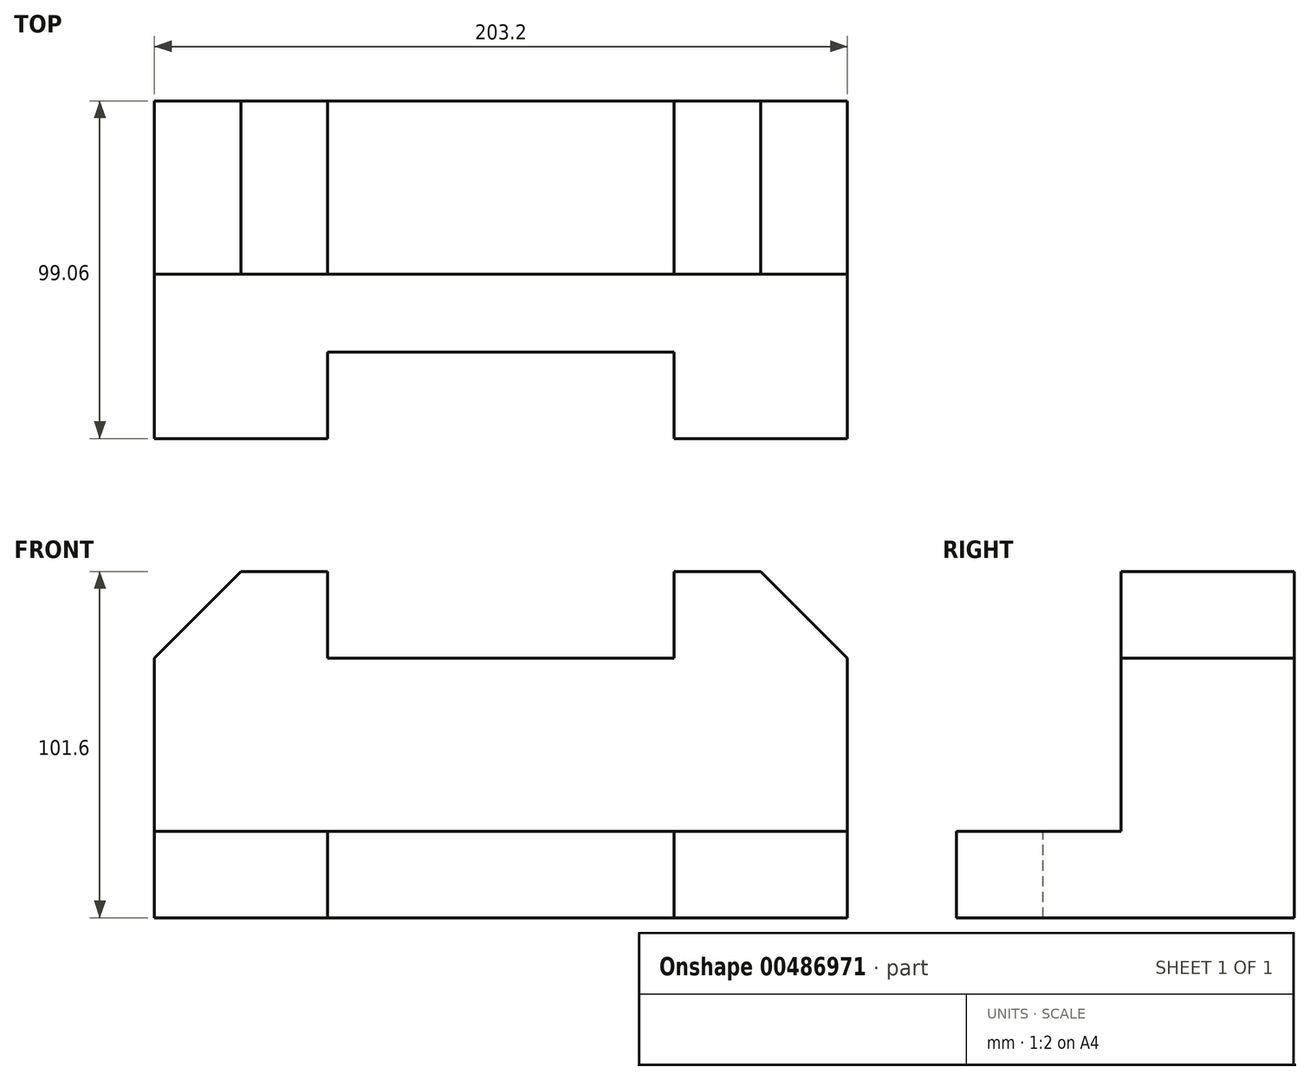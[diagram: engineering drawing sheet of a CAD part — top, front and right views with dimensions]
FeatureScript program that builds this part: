
annotation { "Feature Type Name" : "Feature", "Feature Type Description" : "" }
export const myFeature = defineFeature(function(context is Context, id is Id, definition is map)
    precondition{}
    {
        {
            var Q0;
            Q0=qCreatedBy(makeId("Front.planeOp"),FACE);
            var sketch = newSketch(context, id + "F0", { "sketchPlane" : qUnion([Q0])});
            skLineSegment(sketch, "E0.bottom", {"start": v(0, 0) * mm, "end": v(-203.2, 0) * mm});
            skLineSegment(sketch, "E0.top", {"start": v(0, 76.2) * mm, "end": v(-203.2, 76.2) * mm});
            skLineSegment(sketch, "E0.left", {"start": v(0, 0) * mm, "end": v(0, 76.2) * mm});
            skLineSegment(sketch, "E0.right", {"start": v(-203.2, 0) * mm, "end": v(-203.2, 76.2) * mm});
            skSolve(sketch);
        }
        {
            var Q0;
            Q0=makeQuery(id+"F0.imprint","IMPRINT",FACE,{"disambiguationData":[TD([[makeQuery(id+"F0.imprint","IMPRINT",EDGE,{"derivedFrom":sQuery(id+"F0.wireOp",EDGE,"E0.bottom")}),-1.0]])]});
            extrude(context, id + "F1", {"entities" : qUnion([Q0]), "depth" : 50.8 * mm});
        }
        {
            var Q0;
            Q0=makeQuery(id+"F1.opExtrude","SWEPT_FACE",FACE,{"disambiguationData":[OSD([sQuery(id+"F0.wireOp",EDGE,"E0.top")])]});
            var sketch = newSketch(context, id + "F2", { "sketchPlane" : qUnion([Q0])});
            skLineSegment(sketch, "E1.bottom", {"start": v(0, 0) * mm, "end": v(-50.8, 0) * mm});
            skLineSegment(sketch, "E1.top", {"start": v(0, -50.8) * mm, "end": v(-50.8, -50.8) * mm});
            skLineSegment(sketch, "E1.left", {"start": v(0, 0) * mm, "end": v(0, -50.8) * mm});
            skLineSegment(sketch, "E1.right", {"start": v(-50.8, 0) * mm, "end": v(-50.8, -50.8) * mm});
            skLineSegment(sketch, "E2.bottom", {"start": v(-203.2, 0) * mm, "end": v(-152.4, 0) * mm});
            skLineSegment(sketch, "E2.top", {"start": v(-203.2, -50.8) * mm, "end": v(-152.4, -50.8) * mm});
            skLineSegment(sketch, "E2.left", {"start": v(-203.2, 0) * mm, "end": v(-203.2, -50.8) * mm});
            skLineSegment(sketch, "E2.right", {"start": v(-152.4, 0) * mm, "end": v(-152.4, -50.8) * mm});
            skSolve(sketch);
        }
        {
            var Q0;
            Q0=makeQuery(id+"F2.imprint","IMPRINT",FACE,{"disambiguationData":[TD([[makeQuery(id+"F2.imprint","IMPRINT",EDGE,{"derivedFrom":sQuery(id+"F2.wireOp",EDGE,"E2.bottom")}),1.0]])]});
            var Q1;
            Q1=makeQuery(id+"F2.imprint","IMPRINT",FACE,{"disambiguationData":[TD([[makeQuery(id+"F2.imprint","IMPRINT",EDGE,{"derivedFrom":sQuery(id+"F2.wireOp",EDGE,"E1.bottom")}),1.0]])]});
            extrude(context, id + "F3", {"entities" : qUnion([Q0, Q1]), "operationType" : NewBodyOperationType.ADD, "depth" : 25.4 * mm});
        }
        {
            var Q0;
            Q0=makeQuery(id+"F3.boolean.opBoolean","MERGE",FACE,{"derivedFrom":[makeQuery(id+"F1.opExtrude","CAP_FACE",FACE,{"disambiguationData":[OSD([sQuery(id+"F0.wireOp",EDGE,"E0.bottom"),sQuery(id+"F0.wireOp",EDGE,"E0.top"),sQuery(id+"F0.wireOp",EDGE,"E0.left"),sQuery(id+"F0.wireOp",EDGE,"E0.right")])],"isStart":false}),makeQuery(id+"F3.opExtrude","SWEPT_FACE",FACE,{"disambiguationData":[OSD([sQuery(id+"F2.wireOp",EDGE,"E1.top")])]}),makeQuery(id+"F3.opExtrude","SWEPT_FACE",FACE,{"disambiguationData":[OSD([sQuery(id+"F2.wireOp",EDGE,"E2.top")])]})]});
            var sketch = newSketch(context, id + "F4", { "sketchPlane" : qUnion([Q0])});
            skLineSegment(sketch, "E3.bottom", {"start": v(-203.2, 0) * mm, "end": v(0, 0) * mm});
            skLineSegment(sketch, "E3.top", {"start": v(-203.2, 25.4) * mm, "end": v(0, 25.4) * mm});
            skLineSegment(sketch, "E3.left", {"start": v(-203.2, 0) * mm, "end": v(-203.2, 25.4) * mm});
            skLineSegment(sketch, "E3.right", {"start": v(0, 0) * mm, "end": v(0, 25.4) * mm});
            skSolve(sketch);
        }
        {
            var Q0;
            Q0=makeQuery(id+"F4.imprint","IMPRINT",FACE,{"disambiguationData":[TD([[makeQuery(id+"F4.imprint","IMPRINT",EDGE,{"derivedFrom":sQuery(id+"F4.wireOp",EDGE,"E3.bottom")}),-1.0]])]});
            extrude(context, id + "F5", {"entities" : qUnion([Q0]), "operationType" : NewBodyOperationType.ADD, "depth" : 48.26 * mm});
        }
        {
            var Q0;
            Q0=makeQuery(id+"F5.opExtrude","SWEPT_FACE",FACE,{"disambiguationData":[OSD([sQuery(id+"F4.wireOp",EDGE,"E3.top")])]});
            var sketch = newSketch(context, id + "F6", { "sketchPlane" : qUnion([Q0])});
            skLineSegment(sketch, "E4.bottom", {"start": v(-152.4, -99.06) * mm, "end": v(-50.8, -99.06) * mm});
            skLineSegment(sketch, "E4.top", {"start": v(-152.4, -73.66) * mm, "end": v(-50.8, -73.66) * mm});
            skLineSegment(sketch, "E4.left", {"start": v(-152.4, -99.06) * mm, "end": v(-152.4, -73.66) * mm});
            skLineSegment(sketch, "E4.right", {"start": v(-50.8, -99.06) * mm, "end": v(-50.8, -73.66) * mm});
            skSolve(sketch);
        }
        {
            var Q0;
            Q0=makeQuery(id+"F6.imprint","IMPRINT",FACE,{"disambiguationData":[TD([[makeQuery(id+"F6.imprint","IMPRINT",EDGE,{"derivedFrom":sQuery(id+"F6.wireOp",EDGE,"E4.bottom")}),1.0]])]});
            extrude(context, id + "F7", {"entities" : qUnion([Q0]), "operationType" : NewBodyOperationType.REMOVE, "oppositeDirection" : true, "depth" : 25.4 * mm});
        }
        {
            var Q0;
            Q0=makeQuery(id+"F3.opExtrude","CAP_FACE",FACE,{"disambiguationData":[OSD([sQuery(id+"F2.wireOp",EDGE,"E2.bottom"),sQuery(id+"F2.wireOp",EDGE,"E2.top"),sQuery(id+"F2.wireOp",EDGE,"E2.left"),sQuery(id+"F2.wireOp",EDGE,"E2.right")])],"isStart":false});
            var sketch = newSketch(context, id + "F8", { "sketchPlane" : qUnion([Q0])});
            skLineSegment(sketch, "E5.bottom", {"start": v(-203.2, 0) * mm, "end": v(-177.8, 0) * mm});
            skLineSegment(sketch, "E5.top", {"start": v(-203.2, -50.8) * mm, "end": v(-177.8, -50.8) * mm});
            skLineSegment(sketch, "E5.left", {"start": v(-203.2, 0) * mm, "end": v(-203.2, -50.8) * mm});
            skLineSegment(sketch, "E5.right", {"start": v(-177.8, 0) * mm, "end": v(-177.8, -50.8) * mm});
            skLineSegment(sketch, "E6.bottom", {"start": v(0, 0) * mm, "end": v(-25.4, 0) * mm});
            skLineSegment(sketch, "E6.top", {"start": v(0, -50.8) * mm, "end": v(-25.4, -50.8) * mm});
            skLineSegment(sketch, "E6.left", {"start": v(0, 0) * mm, "end": v(0, -50.8) * mm});
            skLineSegment(sketch, "E6.right", {"start": v(-25.4, 0) * mm, "end": v(-25.4, -50.8) * mm});
            skSolve(sketch);
        }
        {
            var Q0;
            Q0=makeQuery(id+"F8.imprint","IMPRINT",FACE,{"disambiguationData":[TD([[makeQuery(id+"F8.imprint","IMPRINT",EDGE,{"derivedFrom":sQuery(id+"F8.wireOp",EDGE,"E6.bottom")}),1.0]])]});
            var Q1;
            Q1=makeQuery(id+"F8.imprint","IMPRINT",FACE,{"disambiguationData":[TD([[makeQuery(id+"F8.imprint","IMPRINT",EDGE,{"derivedFrom":sQuery(id+"F8.wireOp",EDGE,"E5.bottom")}),1.0]])]});
            extrude(context, id + "F9", {"entities" : qUnion([Q0, Q1]), "operationType" : NewBodyOperationType.REMOVE, "oppositeDirection" : true, "depth" : 25.4 * mm});
        }
        {
            var Q0;
            Q0=makeQuery(id+"F3.boolean.opBoolean","MERGE",FACE,{"derivedFrom":[makeQuery(id+"F1.opExtrude","CAP_FACE",FACE,{"disambiguationData":[OSD([sQuery(id+"F0.wireOp",EDGE,"E0.bottom"),sQuery(id+"F0.wireOp",EDGE,"E0.top"),sQuery(id+"F0.wireOp",EDGE,"E0.left"),sQuery(id+"F0.wireOp",EDGE,"E0.right")])],"isStart":false}),makeQuery(id+"F3.opExtrude","SWEPT_FACE",FACE,{"disambiguationData":[OSD([sQuery(id+"F2.wireOp",EDGE,"E1.top")])]}),makeQuery(id+"F3.opExtrude","SWEPT_FACE",FACE,{"disambiguationData":[OSD([sQuery(id+"F2.wireOp",EDGE,"E2.top")])]})]});
            var sketch = newSketch(context, id + "F10", { "sketchPlane" : qUnion([Q0])});
            skLineSegment(sketch, "E7", {"start": v(-25.4, 101.6) * mm, "end": v(0, 76.2) * mm});
            skLineSegment(sketch, "E8", {"start": v(0, 76.2) * mm, "end": v(-25.4, 76.2) * mm});
            skLineSegment(sketch, "E9", {"start": v(-25.4, 76.2) * mm, "end": v(-25.4, 101.6) * mm});
            skLineSegment(sketch, "E10", {"start": v(-177.8, 101.6) * mm, "end": v(-177.8, 76.2) * mm});
            skLineSegment(sketch, "E11", {"start": v(-177.8, 76.2) * mm, "end": v(-203.2, 76.2) * mm});
            skLineSegment(sketch, "E12", {"start": v(-203.2, 76.2) * mm, "end": v(-177.8, 101.6) * mm});
            skSolve(sketch);
        }
        {
            var Q0;
            Q0=makeQuery(id+"F10.imprint","IMPRINT",FACE,{"disambiguationData":[TD([[makeQuery(id+"F10.imprint","IMPRINT",EDGE,{"derivedFrom":sQuery(id+"F10.wireOp",EDGE,"E7")}),-1.0]])]});
            var Q1;
            Q1=makeQuery(id+"F10.imprint","IMPRINT",FACE,{"disambiguationData":[TD([[makeQuery(id+"F10.imprint","IMPRINT",EDGE,{"derivedFrom":sQuery(id+"F10.wireOp",EDGE,"E10")}),1.0]])]});
            extrude(context, id + "F11", {"entities" : qUnion([Q0, Q1]), "operationType" : NewBodyOperationType.ADD, "oppositeDirection" : true, "depth" : 50.8 * mm});
        }
    });
